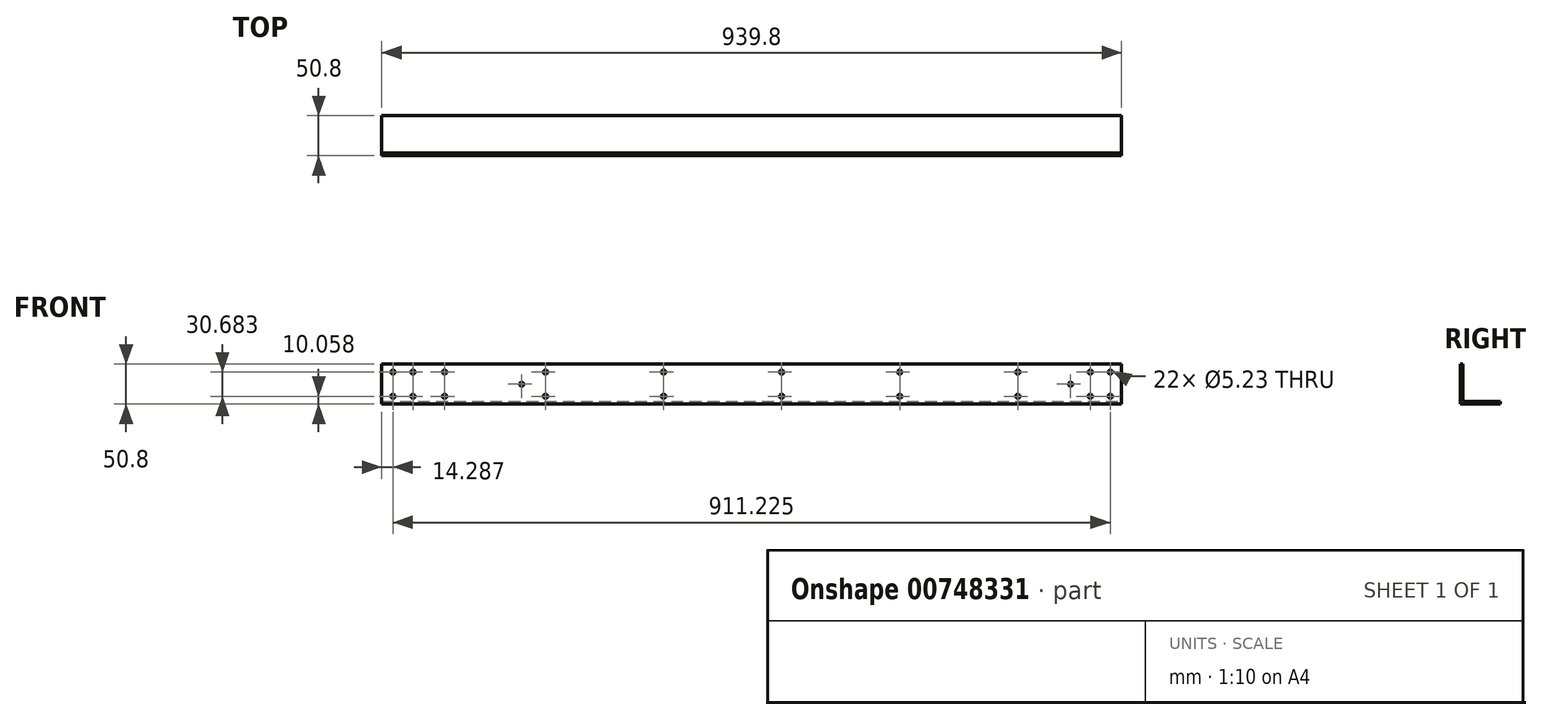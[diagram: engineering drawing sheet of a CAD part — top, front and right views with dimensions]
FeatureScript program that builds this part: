
annotation { "Feature Type Name" : "Feature", "Feature Type Description" : "" }
export const myFeature = defineFeature(function(context is Context, id is Id, definition is map)
    precondition{}
    {
        {
            var Q0;
            Q0=qCreatedBy(makeId("Right.planeOp"),FACE);
            var sketch = newSketch(context, id + "F0", { "sketchPlane" : qUnion([Q0])});
            skLineSegment(sketch, "E0", {"start": v(0, 0) * mm, "end": v(0, -44.45) * mm});
            skLineSegment(sketch, "E1", {"start": v(3.18, -47.62) * mm, "end": v(47.63, -47.62) * mm});
            skLineSegment(sketch, "E2.0", {"start": v(-3.18, -50.8) * mm, "end": v(47.63, -50.8) * mm});
            skLineSegment(sketch, "E2.1", {"start": v(-3.17, 0) * mm, "end": v(-3.18, -50.8) * mm});
            skLineSegment(sketch, "E3", {"start": v(-3.18, 0) * mm, "end": v(0, 0) * mm});
            skLineSegment(sketch, "E4", {"start": v(47.63, -47.62) * mm, "end": v(47.63, -50.8) * mm});
            skPoint(sketch, "E5.visualSharp", {"position": v(0, -47.63) * mm});
            skArc(sketch, "E5.filletArc", {"start": v(0, -44.45) * mm, "mid": v(0.93, -46.7) * mm, "end": v(3.18, -47.63) * mm});
            skSolve(sketch);
        }
        {
            var Q0;
            Q0=makeQuery(id+"F0.imprint","IMPRINT",FACE,{"disambiguationData":[TD([[makeQuery(id+"F0.imprint","IMPRINT",EDGE,{"derivedFrom":sQuery(id+"F0.wireOp",EDGE,"E0")}),-1.0]])]});
            extrude(context, id + "F1", {"entities" : qUnion([Q0]), "oppositeDirection" : true, "depth" : 939.8 * mm, "offsetDistance" : 25.4 * mm});
        }
        {
            var Q0;
            Q0=makeQuery(id+"F1.opExtrude","SWEPT_FACE",FACE,{"disambiguationData":[OSD([sQuery(id+"F0.wireOp",EDGE,"E2.1")])]});
            var sketch = newSketch(context, id + "F2", { "sketchPlane" : qUnion([Q0])});
            skLineSegment(sketch, "E6", {"start": v(0, -25.4) * mm, "end": v(-939.8, -25.4) * mm, "construction": true});
            skLineSegment(sketch, "E7", {"start": v(-431.8, -50.8) * mm, "end": v(-431.8, 0) * mm, "construction": true});
            skLineSegment(sketch, "E8", {"start": v(-14.29, -50.8) * mm, "end": v(-14.29, 0) * mm, "construction": true});
            skCircle(sketch, "E9", {"center": v(-14.29, -40.74) * mm, "radius": 2.62 * mm});
            skCircle(sketch, "E10", {"center": v(-14.29, -10.06) * mm, "radius": 2.62 * mm});
            skLineSegment(sketch, "E11", {"start": v(-925.51, 0) * mm, "end": v(-925.51, -50.8) * mm, "construction": true});
            skCircle(sketch, "E12", {"center": v(-925.51, -40.74) * mm, "radius": 2.62 * mm});
            skCircle(sketch, "E13", {"center": v(-925.51, -10.06) * mm, "radius": 2.62 * mm});
            skLineSegment(sketch, "E14.0", {"start": v(-63.5, -10.06) * mm, "end": v(-850.9, -10.06) * mm, "construction": true});
            skLineSegment(sketch, "E15.0", {"start": v(-63.5, -40.74) * mm, "end": v(-850.9, -40.74) * mm, "construction": true});
            skCircle(sketch, "E16", {"center": v(-431.8, -10.06) * mm, "radius": 2.62 * mm});
            skCircle(sketch, "E17", {"center": v(-431.8, -40.74) * mm, "radius": 2.62 * mm});
            skLineSegment(sketch, "E18.0", {"start": v(-762, -50.8) * mm, "end": v(-762, 0) * mm, "construction": true});
            skLineSegment(sketch, "E19.0", {"start": v(-64.77, -50.8) * mm, "end": v(-64.77, 0) * mm, "construction": true});
            skCircle(sketch, "E20", {"center": v(-64.77, -25.4) * mm, "radius": 2.62 * mm});
            skCircle(sketch, "E21", {"center": v(-762, -25.4) * mm, "radius": 2.62 * mm});
            skLineSegment(sketch, "E22", {"start": v(-900.11, 0) * mm, "end": v(-900.11, -50.8) * mm, "construction": true});
            skCircle(sketch, "E23", {"center": v(-900.11, -10.06) * mm, "radius": 2.62 * mm});
            skCircle(sketch, "E24", {"center": v(-900.11, -40.74) * mm, "radius": 2.62 * mm});
            skLineSegment(sketch, "E25", {"start": v(-39.69, 0) * mm, "end": v(-39.69, -50.8) * mm, "construction": true});
            skCircle(sketch, "E26", {"center": v(-39.69, -10.06) * mm, "radius": 2.62 * mm});
            skCircle(sketch, "E27", {"center": v(-39.69, -40.74) * mm, "radius": 2.62 * mm});
            skLineSegment(sketch, "E28", {"start": v(-859.97, 0) * mm, "end": v(-859.97, -50.8) * mm, "construction": true});
            skCircle(sketch, "E29", {"center": v(-859.97, -10.06) * mm, "radius": 2.62 * mm});
            skCircle(sketch, "E30", {"center": v(-859.97, -40.74) * mm, "radius": 2.62 * mm});
            skLineSegment(sketch, "E31.0", {"start": v(-281.8, -50.8) * mm, "end": v(-281.8, 0) * mm, "construction": true});
            skLineSegment(sketch, "E32.0", {"start": v(-131.8, -50.8) * mm, "end": v(-131.8, 0) * mm, "construction": true});
            skLineSegment(sketch, "E33.0", {"start": v(-581.8, -50.8) * mm, "end": v(-581.8, 0) * mm, "construction": true});
            skLineSegment(sketch, "E34.0", {"start": v(-731.8, -50.8) * mm, "end": v(-731.8, 0) * mm, "construction": true});
            skCircle(sketch, "E35", {"center": v(-731.8, -10.06) * mm, "radius": 2.62 * mm});
            skCircle(sketch, "E36", {"center": v(-731.8, -40.74) * mm, "radius": 2.62 * mm});
            skCircle(sketch, "E37", {"center": v(-581.8, -10.06) * mm, "radius": 2.62 * mm});
            skCircle(sketch, "E38", {"center": v(-581.8, -40.74) * mm, "radius": 2.62 * mm});
            skPoint(sketch, "E38.centerSnap0", {"position": v(-581.8, -25.4) * mm});
            skCircle(sketch, "E39", {"center": v(-281.8, -10.06) * mm, "radius": 2.62 * mm});
            skCircle(sketch, "E40", {"center": v(-281.8, -40.74) * mm, "radius": 2.62 * mm});
            skCircle(sketch, "E41", {"center": v(-131.8, -10.06) * mm, "radius": 2.62 * mm});
            skCircle(sketch, "E42", {"center": v(-131.8, -40.74) * mm, "radius": 2.62 * mm});
            skSolve(sketch);
        }
        {
            var Q0;
            Q0=qSketchRegion(id+"F2",true);
            extrude(context, id + "F3", {"entities" : qUnion([Q0]), "operationType" : NewBodyOperationType.REMOVE, "endBound" : BoundingType.THROUGH_ALL, "oppositeDirection" : true, "depth" : 25.4 * mm, "offsetDistance" : 25.4 * mm});
        }
    });
